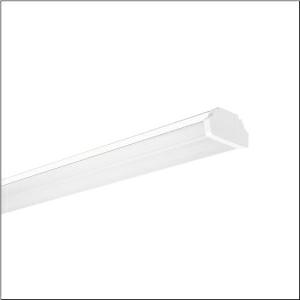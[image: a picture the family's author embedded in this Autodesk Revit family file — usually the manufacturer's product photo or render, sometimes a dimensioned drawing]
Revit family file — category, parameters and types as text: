
# Revit family: dus_r__31_mo_53bd812d2v6085_5279
name_source: partatom
category: Lighting Fixtures
units: mm (PartAtom-declared; Revit-internal decimal feet)

## family parameters
Cut with Voids When Loaded = No
Host = Face
Light Source = No
Part Type = Normal
Room Calculation Point = No
Round Connector Dimension = Use Diameter
Shared = No

## types (1)
- --- (1 x LED, 8960 lm, 61.8 W, 6500K)
    Apparent Load = 62 VA
    CIE Flux Codes = 47 80 95 92 100
    Color Rendering = 80
    Color Temperature = 6500K
    Default Elevation = 1800 mm
    Description = DUS® 31 MO, luminaire insert, of sheet steel, coil coated, white, length: 1.535mm, width: 81mm, height: 90mm, 5x system unit, system units: 307mm, LED rated luminous flux: 8.960lm, light colour: 865, control gear: DALI 2, control gear: ECG DALI, with plug, 5-pole, with phase selection, mains connection: 220..240V, AC, 50/60Hz, rated input power: 62W, through-wiring accessed according to module size, primary optical cover: cover, of PMMA, light emission: direct distribution, primary light characteristic: symmetric, protection rating (complete): IP20, protection rating (LED compartment): IP50, insulation class (complete): insulation class I (protective earthing), certification: CE, ENEC, VDE, UKCA, impact resistance: IK03, permissible ambient temperature for indoor applications: -25..+30°C, corresponds to IFS (International Featured Standards) requirements for safety and quality in the food industry, reducing of maximum allowable ambient temperature of 5°C with ceiling mounting, packaging unit: 1 piece
    Height = 95 mm
    Lamp = 1 x LED
    Lamp Light Flux = 8960 lm
    Lamp Power = 61.8 W
    Lamp count = 1
    Length = 1535 mm
    Luminous efficacy = 145 lm/W
    Manufacturer = Siteco
    ModVariant = No
    Model = 53BD812D2V6085
    Mounting Place = Ceiling
    Mounting Type = Pendant
    Number of Poles = 1
    OnlyDefault = Yes
    Power Factor = 1
    Product Name = DUS® 31 MO
    Product group = luminaire insert
    ProductGroupID = 901
    Protection Class = Protection class I
    Protection Degree = IP 20
    RLX_Detail_Level = 1
    RLX_Emergency_Light_Flux = 0 lm
    RLX_Emergency_Type = 0
    RLX_Emergency_Type_DB = No
    RlxData = <blob elided: 42093 chars, md5=d04a706b>
    Socket = socket
    Standby Power = 0 W
    System Light Flux = 8960 lm
    System Power = 62 W
    Type Comments = factory setting: luminous flux: 100 % | dim-lin: 254 | 500 mA
    Type Image = l_1003451.jpg
    URL = http://relux.com
    VarID = @adj_130695
    Voltage = 0 V
    Weight = 0.00 kg
    Width = 81 mm

## geometry (parser evidence)
native form markers: Blend x4, Sweep x13
no freeform markers — native parametric forms only
